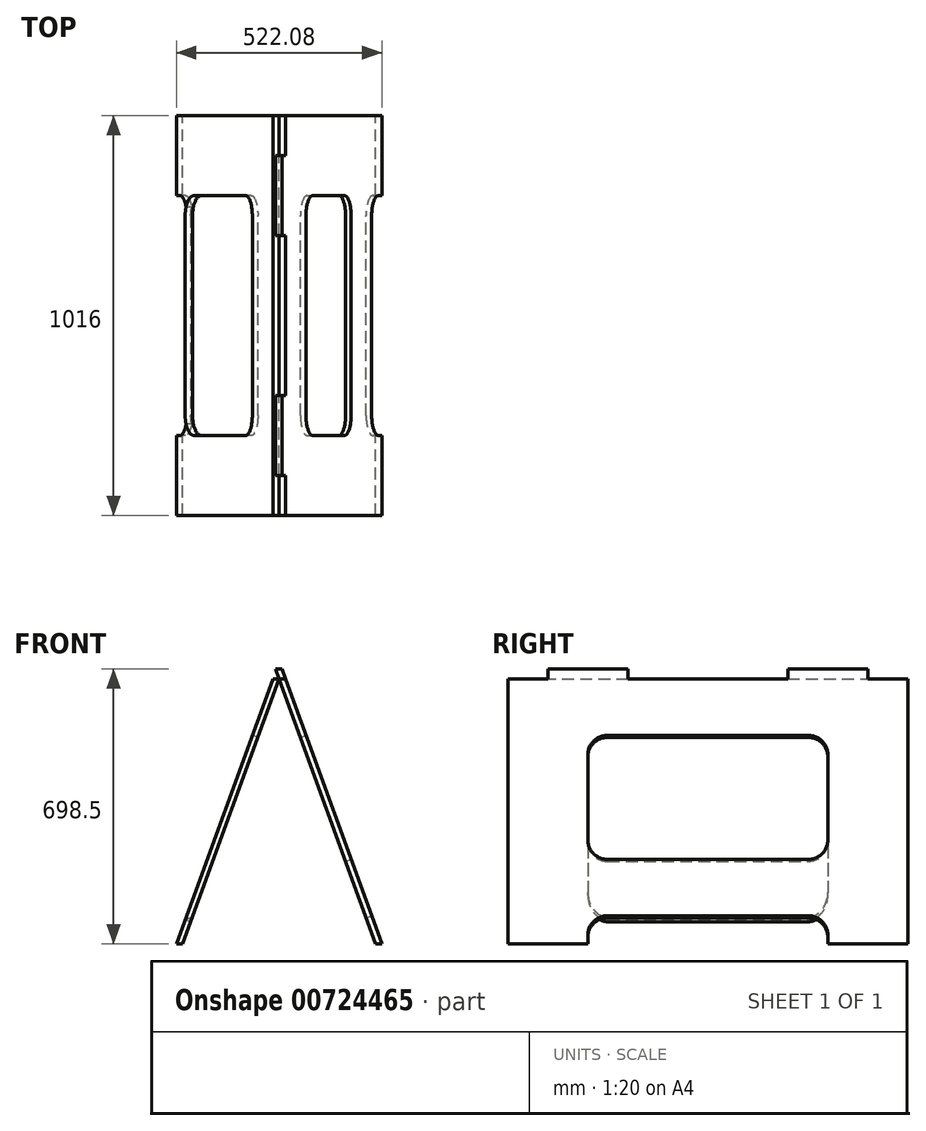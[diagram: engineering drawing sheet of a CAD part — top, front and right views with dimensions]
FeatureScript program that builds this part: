
annotation { "Feature Type Name" : "Feature", "Feature Type Description" : "" }
export const myFeature = defineFeature(function(context is Context, id is Id, definition is map)
    precondition{}
    {
        {
            var Q0;
            Q0=qCreatedBy(makeId("Front.planeOp"),FACE);
            var sketch = newSketch(context, id + "F0", { "sketchPlane" : qUnion([Q0])});
            skLineSegment(sketch, "E0", {"start": v(0, 0) * mm, "end": v(0, -673.1) * mm, "construction": true});
            skLineSegment(sketch, "E1", {"start": v(0, -673.1) * mm, "end": v(-668.78, -673.1) * mm, "construction": true});
            skLineSegment(sketch, "E2", {"start": v(0, -673.1) * mm, "end": v(754.97, -673.1) * mm, "construction": true});
            skLineSegment(sketch, "E3", {"start": v(-668.78, 0) * mm, "end": v(754.97, 0) * mm, "construction": true});
            skLineSegment(sketch, "E4.0", {"start": v(-668.78, 25.4) * mm, "end": v(754.97, 25.4) * mm, "construction": true});
            skLineSegment(sketch, "E5", {"start": v(-9.24, 25.4) * mm, "end": v(244.99, -673.1) * mm});
            skLineSegment(sketch, "E6.0", {"start": v(6.8, 25.4) * mm, "end": v(261.04, -673.1) * mm});
            skLineSegment(sketch, "E7", {"start": v(-9.24, 25.4) * mm, "end": v(6.8, 25.4) * mm});
            skLineSegment(sketch, "E8", {"start": v(244.99, -673.1) * mm, "end": v(261.04, -673.1) * mm});
            skLineSegment(sketch, "E9", {"start": v(0, 0) * mm, "end": v(-244.99, -673.1) * mm});
            skLineSegment(sketch, "E10.0", {"start": v(-16.05, 0) * mm, "end": v(-261.04, -673.1) * mm});
            skLineSegment(sketch, "E11", {"start": v(-261.04, -673.1) * mm, "end": v(-244.99, -673.1) * mm});
            skLineSegment(sketch, "E12", {"start": v(-16.05, 0) * mm, "end": v(0, 0) * mm});
            skSolve(sketch);
        }
        {
            var Q0;
            Q0=makeQuery(id+"F0.imprint","IMPRINT",FACE,{"disambiguationData":[TD([[makeQuery(id+"F0.imprint","IMPRINT",EDGE,{"derivedFrom":sQuery(id+"F0.wireOp",EDGE,"E5")}),1.0]])]});
            extrude(context, id + "F1", {"entities" : qUnion([Q0]), "depth" : 1016 * mm, "offsetDistance" : 25.4 * mm, "symmetric" : true});
        }
        {
            var Q0;
            Q0=makeQuery(id+"F0.imprint","IMPRINT",FACE,{"disambiguationData":[TD([[makeQuery(id+"F0.imprint","IMPRINT",EDGE,{"derivedFrom":sQuery(id+"F0.wireOp",EDGE,"E9")}),-1.0]])]});
            extrude(context, id + "F2", {"entities" : qUnion([Q0]), "depth" : 1016 * mm, "offsetDistance" : 25.4 * mm, "symmetric" : true});
        }
        {
            var Q0;
            Q0=qCreatedBy(makeId("Right.planeOp"),FACE);
            var sketch = newSketch(context, id + "F3", { "sketchPlane" : qUnion([Q0])});
            skLineSegment(sketch, "E13", {"start": v(0, 0) * mm, "end": v(-508, 0) * mm, "construction": true});
            skLineSegment(sketch, "E14", {"start": v(0, 0) * mm, "end": v(508, 0) * mm, "construction": true});
            skLineSegment(sketch, "E15.bottom", {"start": v(0, 0) * mm, "end": v(-203.2, 0) * mm});
            skLineSegment(sketch, "E15.top", {"start": v(0, 25.4) * mm, "end": v(-203.2, 25.4) * mm});
            skLineSegment(sketch, "E15.left", {"start": v(0, 0) * mm, "end": v(0, 25.4) * mm});
            skLineSegment(sketch, "E15.right", {"start": v(-203.2, 0) * mm, "end": v(-203.2, 25.4) * mm});
            skLineSegment(sketch, "E16.bottom", {"start": v(-508, 0) * mm, "end": v(-406.4, 0) * mm});
            skLineSegment(sketch, "E16.top", {"start": v(-508, 25.4) * mm, "end": v(-406.4, 25.4) * mm});
            skLineSegment(sketch, "E16.left", {"start": v(-508, 0) * mm, "end": v(-508, 25.4) * mm});
            skLineSegment(sketch, "E16.right", {"start": v(-406.4, 0) * mm, "end": v(-406.4, 25.4) * mm});
            skLineSegment(sketch, "E17.bottom", {"start": v(0, 0) * mm, "end": v(203.2, 0) * mm});
            skLineSegment(sketch, "E17.top", {"start": v(0, 25.4) * mm, "end": v(203.2, 25.4) * mm});
            skLineSegment(sketch, "E17.right", {"start": v(203.2, 0) * mm, "end": v(203.2, 25.4) * mm});
            skLineSegment(sketch, "E18.bottom", {"start": v(508, 0) * mm, "end": v(406.4, 0) * mm});
            skLineSegment(sketch, "E18.top", {"start": v(508, 25.4) * mm, "end": v(406.4, 25.4) * mm});
            skLineSegment(sketch, "E18.left", {"start": v(508, 0) * mm, "end": v(508, 25.4) * mm});
            skLineSegment(sketch, "E18.right", {"start": v(406.4, 0) * mm, "end": v(406.4, 25.4) * mm});
            skSolve(sketch);
        }
        {
            var Q0;
            Q0 = qSketchRegion(id + "F3", true);
            extrude(context, id + "F4", {"entities" : qUnion([Q0]), "operationType" : NewBodyOperationType.REMOVE, "oppositeDirection" : true, "depth" : 50.8 * mm, "offsetDistance" : 25.4 * mm, "symmetric" : true});
        }
        {
            var Q0;
            Q0=makeQuery(id+"F1.opExtrude","SWEPT_FACE",FACE,{"disambiguationData":[OSD([sQuery(id+"F0.wireOp",EDGE,"E6.0")])]});
            var sketch = newSketch(context, id + "F5", { "sketchPlane" : qUnion([Q0])});
            skLineSegment(sketch, "E19.bottom", {"start": v(-304.8, -721.79) * mm, "end": v(304.8, -721.79) * mm});
            skLineSegment(sketch, "E19.top", {"start": v(-254, -645.59) * mm, "end": v(254, -645.59) * mm});
            skLineSegment(sketch, "E19.left", {"start": v(-304.8, -721.79) * mm, "end": v(-304.8, -696.39) * mm});
            skLineSegment(sketch, "E19.right", {"start": v(304.8, -721.79) * mm, "end": v(304.8, -696.39) * mm});
            skPoint(sketch, "E20.visualSharp", {"position": v(-304.8, -645.59) * mm});
            skArc(sketch, "E20.filletArc", {"start": v(-254, -645.59) * mm, "mid": v(-289.92, -660.47) * mm, "end": v(-304.8, -696.39) * mm});
            skPoint(sketch, "E21.visualSharp", {"position": v(304.8, -645.59) * mm});
            skArc(sketch, "E21.filletArc", {"start": v(304.8, -696.39) * mm, "mid": v(289.92, -660.47) * mm, "end": v(254, -645.59) * mm});
            skSolve(sketch);
        }
        {
            var Q0;
            Q0=makeQuery(id+"F5.imprint","IMPRINT",FACE,{"disambiguationData":[TD([[makeQuery(id+"F5.imprint","IMPRINT",EDGE,{"derivedFrom":sQuery(id+"F5.wireOp",EDGE,"E19.bottom")}),1.0]])]});
            extrude(context, id + "F6", {"entities" : qUnion([Q0]), "operationType" : NewBodyOperationType.REMOVE, "endBound" : BoundingType.THROUGH_ALL, "oppositeDirection" : true, "depth" : 25.4 * mm, "offsetDistance" : 25.4 * mm});
        }
        {
            var Q0;
            Q0=makeQuery(id+"F1.opExtrude","SWEPT_FACE",FACE,{"disambiguationData":[OSD([sQuery(id+"F0.wireOp",EDGE,"E6.0")])]});
            var sketch = newSketch(context, id + "F7", { "sketchPlane" : qUnion([Q0])});
            skLineSegment(sketch, "E22.bottom", {"start": v(-254, -157.89) * mm, "end": v(254, -157.89) * mm});
            skLineSegment(sketch, "E22.top", {"start": v(-254, -493.19) * mm, "end": v(254, -493.19) * mm});
            skLineSegment(sketch, "E22.left", {"start": v(-304.8, -208.69) * mm, "end": v(-304.8, -442.39) * mm});
            skLineSegment(sketch, "E22.right", {"start": v(304.8, -208.69) * mm, "end": v(304.8, -442.39) * mm});
            skPoint(sketch, "E23.visualSharp", {"position": v(-304.8, -157.89) * mm});
            skArc(sketch, "E23.filletArc", {"start": v(-254, -157.89) * mm, "mid": v(-289.92, -172.77) * mm, "end": v(-304.8, -208.69) * mm});
            skPoint(sketch, "E24.visualSharp", {"position": v(304.8, -157.89) * mm});
            skArc(sketch, "E24.filletArc", {"start": v(304.8, -208.69) * mm, "mid": v(289.92, -172.77) * mm, "end": v(254, -157.89) * mm});
            skPoint(sketch, "E25.visualSharp", {"position": v(-304.8, -493.19) * mm});
            skArc(sketch, "E25.filletArc", {"start": v(-304.8, -442.39) * mm, "mid": v(-289.92, -478.3) * mm, "end": v(-254, -493.19) * mm});
            skPoint(sketch, "E26.visualSharp", {"position": v(304.8, -493.19) * mm});
            skArc(sketch, "E26.filletArc", {"start": v(254, -493.19) * mm, "mid": v(289.92, -478.3) * mm, "end": v(304.8, -442.39) * mm});
            skSolve(sketch);
        }
        {
            var Q0;
            Q0=makeQuery(id+"F7.imprint","IMPRINT",FACE,{"disambiguationData":[TD([[makeQuery(id+"F7.imprint","IMPRINT",EDGE,{"derivedFrom":sQuery(id+"F7.wireOp",EDGE,"E22.bottom")}),-1.0]])]});
            extrude(context, id + "F8", {"entities" : qUnion([Q0]), "operationType" : NewBodyOperationType.REMOVE, "endBound" : BoundingType.THROUGH_ALL, "oppositeDirection" : true, "depth" : 25.4 * mm, "offsetDistance" : 25.4 * mm});
        }
        {
            var Q0;
            Q0=makeQuery(id+"F2.opExtrude","SWEPT_FACE",FACE,{"disambiguationData":[OSD([sQuery(id+"F0.wireOp",EDGE,"E10.0")])]});
            var sketch = newSketch(context, id + "F9", { "sketchPlane" : qUnion([Q0])});
            skLineSegment(sketch, "E27.bottom", {"start": v(-304.8, -721.79) * mm, "end": v(304.8, -721.79) * mm});
            skLineSegment(sketch, "E27.top", {"start": v(-254, -645.59) * mm, "end": v(254, -645.59) * mm});
            skLineSegment(sketch, "E27.left", {"start": v(-304.8, -721.79) * mm, "end": v(-304.8, -696.39) * mm});
            skLineSegment(sketch, "E27.right", {"start": v(304.8, -721.79) * mm, "end": v(304.8, -696.39) * mm});
            skPoint(sketch, "E28.visualSharp", {"position": v(-304.8, -645.59) * mm});
            skArc(sketch, "E28.filletArc", {"start": v(-254, -645.59) * mm, "mid": v(-289.92, -660.47) * mm, "end": v(-304.8, -696.39) * mm});
            skPoint(sketch, "E29.visualSharp", {"position": v(304.8, -645.59) * mm});
            skArc(sketch, "E29.filletArc", {"start": v(304.8, -696.39) * mm, "mid": v(289.92, -660.47) * mm, "end": v(254, -645.59) * mm});
            skLineSegment(sketch, "E30.bottom", {"start": v(-254, -157.89) * mm, "end": v(254, -157.89) * mm});
            skLineSegment(sketch, "E30.top", {"start": v(-254, -493.19) * mm, "end": v(254, -493.19) * mm});
            skLineSegment(sketch, "E30.left", {"start": v(-304.8, -208.69) * mm, "end": v(-304.8, -442.39) * mm});
            skLineSegment(sketch, "E30.right", {"start": v(304.8, -208.69) * mm, "end": v(304.8, -442.39) * mm});
            skPoint(sketch, "E31.visualSharp", {"position": v(-304.8, -157.89) * mm});
            skArc(sketch, "E31.filletArc", {"start": v(-254, -157.89) * mm, "mid": v(-289.92, -172.77) * mm, "end": v(-304.8, -208.69) * mm});
            skPoint(sketch, "E32.visualSharp", {"position": v(-304.8, -493.19) * mm});
            skArc(sketch, "E32.filletArc", {"start": v(-304.8, -442.39) * mm, "mid": v(-289.92, -478.3) * mm, "end": v(-254, -493.19) * mm});
            skPoint(sketch, "E33.visualSharp", {"position": v(304.8, -493.19) * mm});
            skArc(sketch, "E33.filletArc", {"start": v(254, -493.19) * mm, "mid": v(289.92, -478.3) * mm, "end": v(304.8, -442.39) * mm});
            skPoint(sketch, "E34.visualSharp", {"position": v(304.8, -157.89) * mm});
            skArc(sketch, "E34.filletArc", {"start": v(304.8, -208.69) * mm, "mid": v(289.92, -172.77) * mm, "end": v(254, -157.89) * mm});
            skSolve(sketch);
        }
        {
            var Q0;
            Q0=makeQuery(id+"F9.imprint","IMPRINT",FACE,{"disambiguationData":[TD([[makeQuery(id+"F9.imprint","IMPRINT",EDGE,{"derivedFrom":sQuery(id+"F9.wireOp",EDGE,"E30.bottom")}),-1.0]])]});
            var Q1;
            Q1=makeQuery(id+"F9.imprint","IMPRINT",FACE,{"disambiguationData":[TD([[makeQuery(id+"F9.imprint","IMPRINT",EDGE,{"derivedFrom":sQuery(id+"F9.wireOp",EDGE,"E27.bottom")}),-1.0]])]});
            extrude(context, id + "F10", {"entities" : qUnion([Q0, Q1]), "operationType" : NewBodyOperationType.REMOVE, "endBound" : BoundingType.THROUGH_ALL, "oppositeDirection" : true, "depth" : 25.4 * mm, "offsetDistance" : 25.4 * mm});
        }
    });
